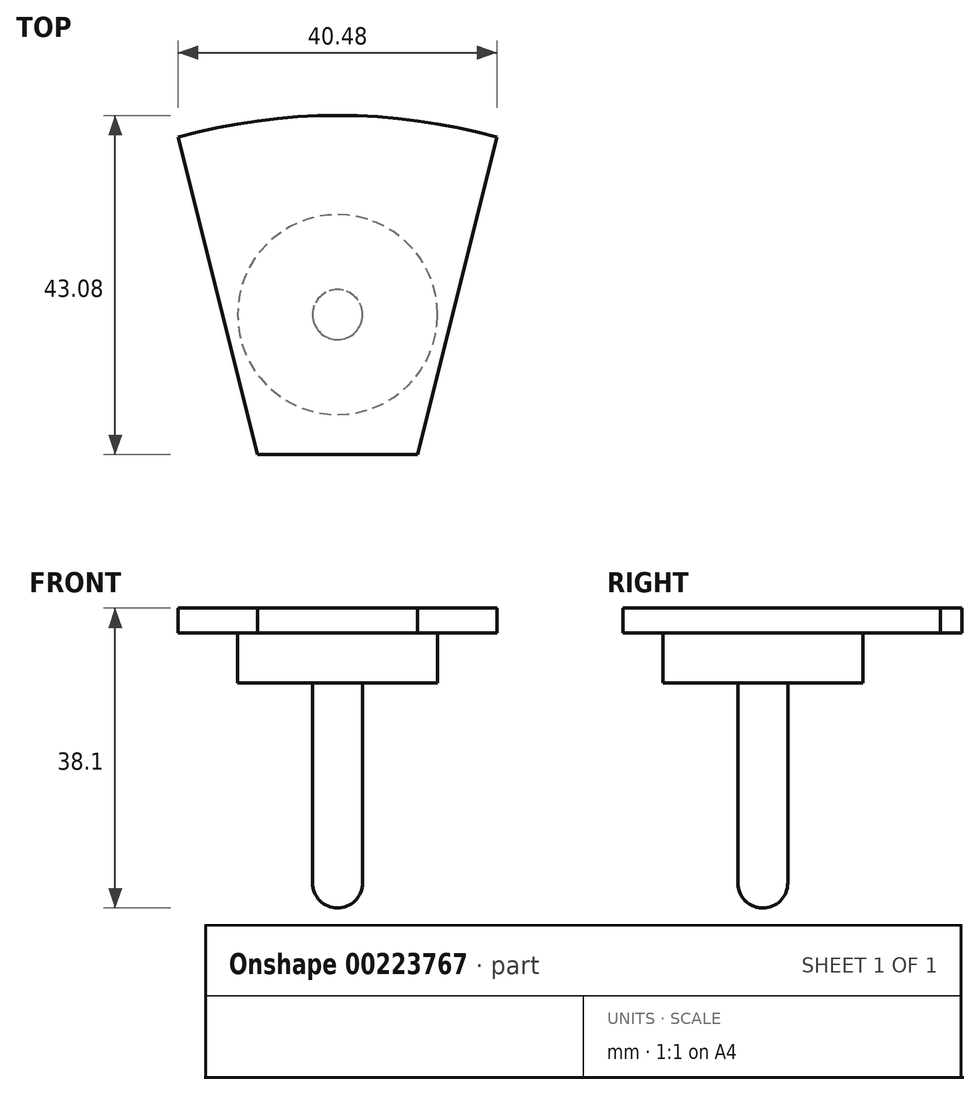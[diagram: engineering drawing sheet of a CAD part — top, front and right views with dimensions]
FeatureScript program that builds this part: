
annotation { "Feature Type Name" : "Feature", "Feature Type Description" : "" }
export const myFeature = defineFeature(function(context is Context, id is Id, definition is map)
    precondition{}
    {
        {
            var Q0;
            Q0=qCreatedBy(makeId("Top.planeOp"),FACE);
            var sketch = newSketch(context, id + "F0", { "sketchPlane" : qUnion([Q0])});
            skCircle(sketch, "E0", {"center": v(0, 0) * mm, "radius": 12.7 * mm});
            skSolve(sketch);
        }
        {
            var Q0;
            Q0 = qSketchRegion(id + "F0", true);
            extrude(context, id + "F1", {"entities" : qUnion([Q0]), "depth" : 6.35 * mm});
        }
        {
            var Q0;
            Q0=makeQuery(id+"F1.opExtrude","CAP_FACE",FACE,{"disambiguationData":[OSD([sQuery(id+"F0.wireOp",EDGE,"E0")])],"isStart":true});
            var sketch = newSketch(context, id + "F2", { "sketchPlane" : qUnion([Q0])});
            skCircle(sketch, "E1", {"center": v(0, 0) * mm, "radius": 3.18 * mm});
            skSolve(sketch);
        }
        {
            var Q0;
            Q0 = qSketchRegion(id + "F2", true);
            extrude(context, id + "F3", {"entities" : qUnion([Q0]), "operationType" : NewBodyOperationType.ADD, "depth" : 25.4 * mm});
        }
        {
            var Q0;
            Q0=qCreatedBy(makeId("Right.planeOp"),FACE);
            var sketch = newSketch(context, id + "F4", { "sketchPlane" : qUnion([Q0])});
            skLineSegment(sketch, "E2", {"start": v(0, 0) * mm, "end": v(0, -25.4) * mm, "construction": true});
            skLineSegment(sketch, "E3", {"start": v(0, -25.4) * mm, "end": v(-3.17, -25.4) * mm});
            skArc(sketch, "E4", {"start": v(-3.17, -25.4) * mm, "mid": v(-2.25, -27.65) * mm, "end": v(0, -28.57) * mm});
            skLineSegment(sketch, "E5", {"start": v(0, -25.4) * mm, "end": v(0, -28.57) * mm});
            skSolve(sketch);
        }
        {
            var Q0;
            Q0 = qSketchRegion(id + "F4", true);
            var Q1;
            Q1=sQuery(id+"F4.wireOp",EDGE,"E2");
            revolve(context, id + "F5", {"operationType" : NewBodyOperationType.ADD, "entities" : qUnion([Q0]), "axis" : qUnion([Q1]), "revolveType" : RevolveType.FULL});
        }
        {
            var Q0;
            Q0=makeQuery(id+"F1.opExtrude","CAP_FACE",FACE,{"disambiguationData":[OSD([sQuery(id+"F0.wireOp",EDGE,"E0")])],"isStart":false});
            var sketch = newSketch(context, id + "F6", { "sketchPlane" : qUnion([Q0])});
            skLineSegment(sketch, "E6", {"start": v(0, 0) * mm, "end": v(0, -17.78) * mm, "construction": true});
            skLineSegment(sketch, "E7", {"start": v(0, -17.78) * mm, "end": v(-10.16, -17.78) * mm});
            skLineSegment(sketch, "E8", {"start": v(-19.05, 17.78) * mm, "end": v(0, 17.78) * mm, "construction": true});
            skLineSegment(sketch, "E9", {"start": v(0, 17.78) * mm, "end": v(0, 0) * mm, "construction": true});
            skLineSegment(sketch, "E10.MirrorCS", {"start": v(0, -17.78) * mm, "end": v(10.16, -17.78) * mm});
            skLineSegment(sketch, "E11.MirrorCS", {"start": v(10.16, -17.78) * mm, "end": v(19.05, 17.78) * mm});
            skLineSegment(sketch, "E12", {"start": v(0, -17.78) * mm, "end": v(0, -50.9) * mm, "construction": true});
            skArc(sketch, "E13", {"start": v(20.24, 22.56) * mm, "mid": v(0, 25.3) * mm, "end": v(-20.24, 22.56) * mm});
            skLineSegment(sketch, "E14", {"start": v(-10.16, -17.78) * mm, "end": v(-19.05, 17.78) * mm});
            skLineSegment(sketch, "E15", {"start": v(-19.05, 17.78) * mm, "end": v(-20.24, 22.56) * mm});
            skLineSegment(sketch, "E16.MirrorCS", {"start": v(19.05, 17.78) * mm, "end": v(20.24, 22.56) * mm});
            skLineSegment(sketch, "E17", {"start": v(0, 17.78) * mm, "end": v(19.05, 17.78) * mm, "construction": true});
            skSolve(sketch);
        }
        {
            var Q0;
            Q0 = qSketchRegion(id + "F6", true);
            extrude(context, id + "F7", {"entities" : qUnion([Q0]), "operationType" : NewBodyOperationType.ADD, "depth" : 3.17 * mm});
        }
    });
